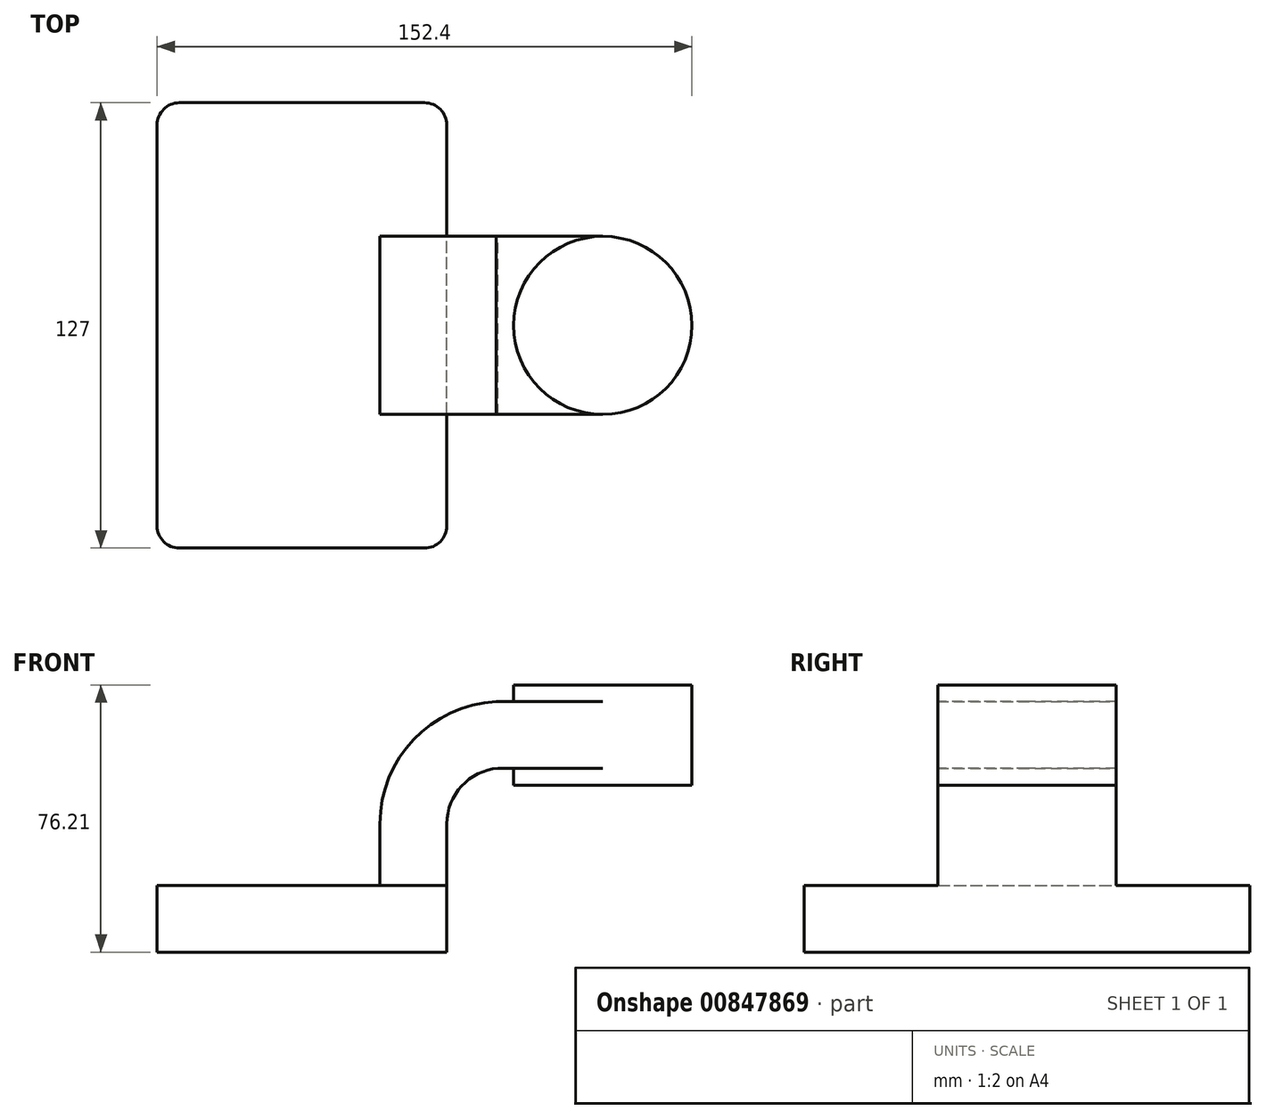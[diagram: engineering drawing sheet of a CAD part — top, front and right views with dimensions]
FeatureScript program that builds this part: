
annotation { "Feature Type Name" : "Feature", "Feature Type Description" : "" }
export const myFeature = defineFeature(function(context is Context, id is Id, definition is map)
    precondition{}
    {
        {
            var Q0;
            Q0=qCreatedBy(makeId("Front.planeOp"),FACE);
            var sketch = newSketch(context, id + "F0", { "sketchPlane" : qUnion([Q0])});
            skLineSegment(sketch, "E0.bottom", {"start": v(41.28, -9.52) * mm, "end": v(-41.28, -9.53) * mm});
            skLineSegment(sketch, "E0.top", {"start": v(41.28, 9.53) * mm, "end": v(-41.28, 9.53) * mm});
            skLineSegment(sketch, "E0.left", {"start": v(41.28, -9.52) * mm, "end": v(41.28, 9.53) * mm});
            skLineSegment(sketch, "E0.right", {"start": v(-41.28, -9.53) * mm, "end": v(-41.28, 9.53) * mm});
            skPoint(sketch, "E0.middle", {"position": v(0, 0) * mm});
            skLineSegment(sketch, "E1.bottom", {"start": v(111.13, 38.1) * mm, "end": v(60.32, 38.1) * mm});
            skLineSegment(sketch, "E1.top", {"start": v(111.13, 66.68) * mm, "end": v(60.32, 66.68) * mm});
            skLineSegment(sketch, "E1.left", {"start": v(111.13, 38.1) * mm, "end": v(111.13, 66.68) * mm});
            skLineSegment(sketch, "E1.right", {"start": v(60.32, 38.1) * mm, "end": v(60.32, 66.68) * mm});
            skPoint(sketch, "E1.middle", {"position": v(85.73, 52.39) * mm});
            skLineSegment(sketch, "E2", {"start": v(41.28, 9.53) * mm, "end": v(41.28, 27.05) * mm});
            skArc(sketch, "E3", {"start": v(41.27, 27.05) * mm, "mid": v(45.5, 37.82) * mm, "end": v(55.9, 42.88) * mm});
            skLineSegment(sketch, "E4", {"start": v(55.9, 42.88) * mm, "end": v(85.73, 42.88) * mm});
            skPoint(sketch, "E4.endSnap0", {"position": v(85.73, 38.1) * mm});
            skLineSegment(sketch, "E5.0", {"start": v(55.3, 61.93) * mm, "end": v(85.73, 61.93) * mm});
            skArc(sketch, "E5.1", {"start": v(22.23, 27.05) * mm, "mid": v(31.8, 51.08) * mm, "end": v(55.3, 61.93) * mm});
            skLineSegment(sketch, "E5.2", {"start": v(22.22, 9.53) * mm, "end": v(22.22, 27.05) * mm});
            skLineSegment(sketch, "E6", {"start": v(85.73, 38.1) * mm, "end": v(85.73, 66.68) * mm});
            skFitSpline(sketch, "E7", {"points": [v(-41.28, 9.53) * mm, v(55.3, 61.93) * mm], "startDerivative": vector(0, 51.73) * mm, "endDerivative": vector(60.44, 0) * mm});
            skSolve(sketch);
        }
        {
            var Q0;
            Q0=makeQuery(id+"F0.imprint","IMPRINT",FACE,{"disambiguationData":[TD([[makeQuery(id+"F0.imprint","IMPRINT",EDGE,{"derivedFrom":sQuery(id+"F0.wireOp",EDGE,"E0.bottom")}),-1.0]])]});
            extrude(context, id + "F1", {"entities" : qUnion([Q0]), "endBound" : BoundingType.SYMMETRIC, "depth" : 127 * mm, "offsetDistance" : 25.4 * mm});
        }
        {
            var Q0;
            {var subQ1=sQuery(id+"F0.wireOp",EDGE,"E2");Q0=makeQuery(id+"F0.imprint","IMPRINT",FACE,{"disambiguationData":[TD([[makeQuery(id+"F0.imprint","IMPRINT",EDGE,{"derivedFrom":subQ1}),1.0]])]});}
            var Q1;
            {var subQ0=sQuery(id+"F0.wireOp",EDGE,"E4");var subQ1=sQuery(id+"F0.wireOp",EDGE,"E1.right");var subQ2=makeQuery(id+"F0.imprint","INTERSECT",VERTEX,{"derivedFrom":[subQ1,subQ0]});Q1=makeQuery(id+"F0.imprint","IMPRINT",FACE,{"disambiguationData":[TD([[makeQuery(id+"F0.imprint","IMPRINT",EDGE,{"disambiguationData":[TD([[subQ2,-1.0]])],"derivedFrom":subQ1}),-1.0]])]});}
            extrude(context, id + "F2", {"entities" : qUnion([Q0, Q1]), "operationType" : NewBodyOperationType.ADD, "endBound" : BoundingType.SYMMETRIC, "depth" : 50.8 * mm, "offsetDistance" : 25.4 * mm});
        }
        {
            var Q0;
            Q0=makeQuery(id+"F0.imprint","IMPRINT",FACE,{"disambiguationData":[TD([[makeQuery(id+"F0.imprint","IMPRINT",EDGE,{"derivedFrom":sQuery(id+"F0.wireOp",EDGE,"E5.1")}),1.0]])]});
            extrude(context, id + "F3", {"entities" : qUnion([Q0]), "operationType" : NewBodyOperationType.ADD, "endBound" : BoundingType.SYMMETRIC, "depth" : 15.88 * mm, "offsetDistance" : 25.4 * mm});
        }
        {
            var Q0;
            {var subQ4=sQuery(id+"F0.wireOp",EDGE,"E1.left");Q0=makeQuery(id+"F0.imprint","IMPRINT",FACE,{"disambiguationData":[TD([[makeQuery(id+"F0.imprint","IMPRINT",EDGE,{"derivedFrom":subQ4}),1.0]])]});}
            var Q1;
            Q1=sQuery(id+"F0.wireOp",EDGE,"E6");
            revolve(context, id + "F4", {"operationType" : NewBodyOperationType.ADD, "surfaceOperationType" : NewSurfaceOperationType.NEW, "entities" : qUnion([Q0]), "axis" : qUnion([Q1]), "revolveType" : RevolveType.FULL});
        }
        {
            var Q0;
            Q0=makeQuery(id+"F1.opExtrude","CAP_EDGE",EDGE,{"disambiguationData":[OSD([sQuery(id+"F0.wireOp",EDGE,"E0.left")])],"isStart":false});
            var Q1;
            Q1=makeQuery(id+"F1.opExtrude","CAP_EDGE",EDGE,{"disambiguationData":[OSD([sQuery(id+"F0.wireOp",EDGE,"E0.right")])],"isStart":false});
            var Q2;
            Q2=makeQuery(id+"F1.opExtrude","CAP_EDGE",EDGE,{"disambiguationData":[OSD([sQuery(id+"F0.wireOp",EDGE,"E0.left")])],"isStart":true});
            var Q3;
            Q3=makeQuery(id+"F1.opExtrude","CAP_EDGE",EDGE,{"disambiguationData":[OSD([sQuery(id+"F0.wireOp",EDGE,"E0.right")])],"isStart":true});
            fillet(context, id + "F5", {"entities" : qUnion([Q0, Q1, Q2, Q3]), "radius" : 6.35 * mm, "tangentPropagation" : true, "allowEdgeOverflow" : false});
        }
    });
